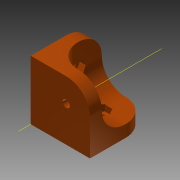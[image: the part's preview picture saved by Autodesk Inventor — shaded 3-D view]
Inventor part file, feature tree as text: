
AUTODESK INVENTOR PART (.ipt)
format: ipt  version: 2013 (Build 170138000, 138)  size: 163,328 bytes
history: native  units: mm
features: extrude x5, sketch x5, other x1, fillet x1, pattern_circular x1
ambient origin geometry x8: Origin, YZ Plane, XZ Plane, XY Plane, X Axis, Y Axis, Z Axis, Center Point
bodies: Solid1 (feature_tree)
feature tree (13):
  extrude  "Extrusion1"  Depth=5.0mm TaperAngle=0.0deg
  extrude  "Extrusion2"  Depth=5.0mm TaperAngle=0.0deg
  extrude  "Extrusion3"  Depth=3.1mm
  other  "Work Axis1"
  fillet  "Fillet2"  Radius=10.0mm
  extrude  "Extrusion6"  Depth=5.0mm TaperAngle=0.0deg
  extrude  "Extrusion7"  [1 undecoded]
  pattern_circular  "Circular Pattern2"  [2 undecoded]
  sketch  "Sketch1"  dims[d0=25.0mm d2=5.0mm d3=0.0mm]
  sketch  "Sketch2"  dims[d4=5.0mm d5=0.0mm d6=5.0mm d7=0.0mm]
  sketch  "Sketch3"  dims[d19=10.0mm d20=3.1mm d22=10.0mm d23=0.0mm]
  sketch  "Sketch6"  dims[d24=5.6mm d25=5.0mm d26=0.0mm]
  sketch  "Sketch7"  dims[d27=30.0mm d28=360.0deg]
note: 3 required parameter values undecoded (feature->parameter linkage not recoverable at this tier; creation-order binding heuristic only, values carry confidence <= 0.55)
